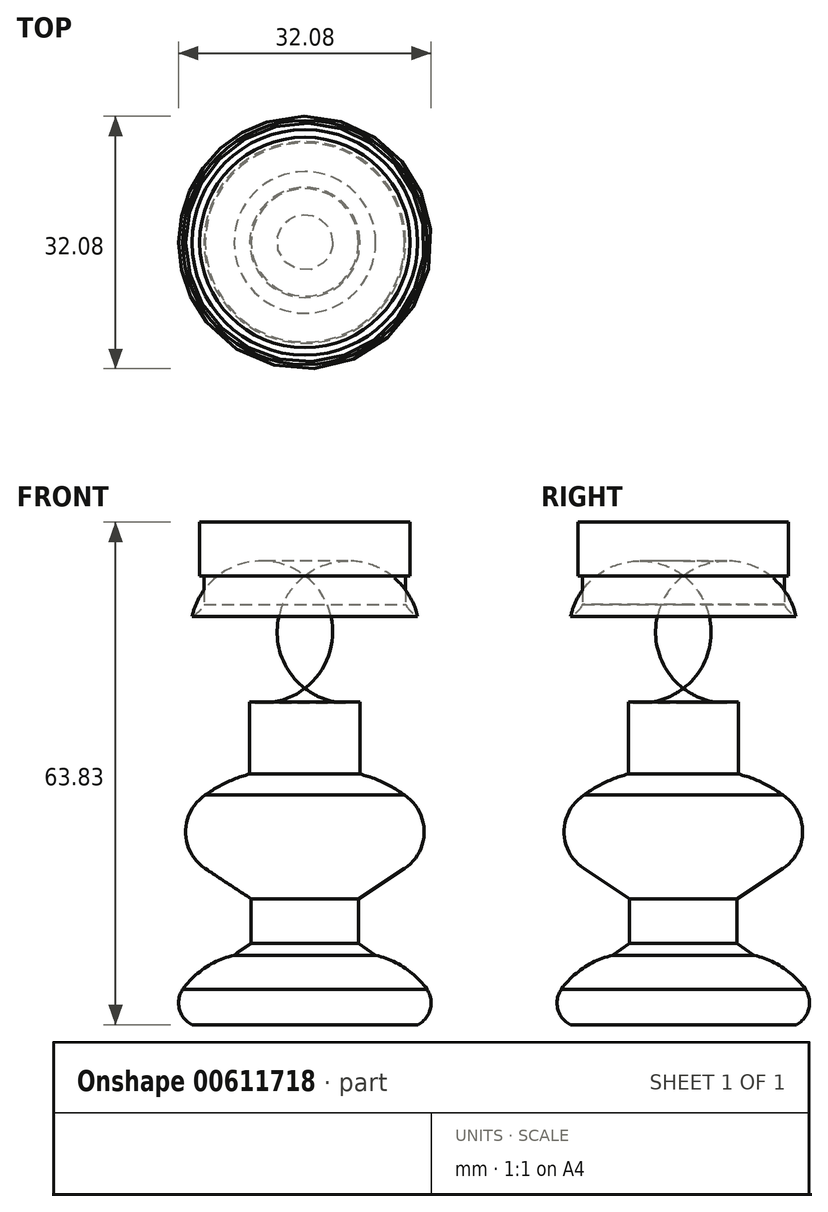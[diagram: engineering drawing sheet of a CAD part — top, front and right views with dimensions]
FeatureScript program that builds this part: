
annotation { "Feature Type Name" : "Feature", "Feature Type Description" : "" }
export const myFeature = defineFeature(function(context is Context, id is Id, definition is map)
    precondition{}
    {
        {
            var Q0;
            Q0=qCreatedBy(makeId("Front.planeOp"),FACE);
            var sketch = newSketch(context, id + "F0", { "sketchPlane" : qUnion([Q0])});
            skLineSegment(sketch, "E0", {"start": v(0, -25.19) * mm, "end": v(-14.34, -25.19) * mm});
            skArc(sketch, "E1", {"start": v(-15.5, -20.69) * mm, "mid": v(-15.94, -23.2) * mm, "end": v(-14.34, -25.19) * mm});
            skArc(sketch, "E2", {"start": v(-9, -16.37) * mm, "mid": v(-12.63, -17.95) * mm, "end": v(-15.5, -20.69) * mm});
            skLineSegment(sketch, "E3", {"start": v(-7, 6.65) * mm, "end": v(-7, 15.79) * mm});
            skArc(sketch, "E4", {"start": v(-14.32, 26.67) * mm, "mid": v(-13, 19.65) * mm, "end": v(-7, 15.79) * mm});
            skArc(sketch, "E5", {"start": v(-14.32, 26.67) * mm, "mid": v(-13.43, 27.3) * mm, "end": v(-12.8, 28.22) * mm});
            skLineSegment(sketch, "E6", {"start": v(-12.8, 28.22) * mm, "end": v(-12.8, 31.52) * mm});
            skArc(sketch, "E7", {"start": v(-12.8, 31.52) * mm, "mid": v(-13, 31.83) * mm, "end": v(-13.36, 31.79) * mm});
            skLineSegment(sketch, "E8", {"start": v(-13.36, 31.79) * mm, "end": v(-13.36, 38.64) * mm});
            skLineSegment(sketch, "E9", {"start": v(-13.36, 38.64) * mm, "end": v(0, 38.64) * mm});
            skLineSegment(sketch, "E10", {"start": v(-9, -16.37) * mm, "end": v(-6.82, -14.84) * mm});
            skLineSegment(sketch, "E11", {"start": v(-6.82, -14.84) * mm, "end": v(-6.82, -9.2) * mm});
            skLineSegment(sketch, "E12", {"start": v(-6.82, -9.2) * mm, "end": v(-12.64, -5.35) * mm});
            skArc(sketch, "E13", {"start": v(-12.64, 3.97) * mm, "mid": v(-15.16, -0.7) * mm, "end": v(-12.64, -5.35) * mm});
            skArc(sketch, "E14", {"start": v(-7, 6.65) * mm, "mid": v(-9.95, 5.58) * mm, "end": v(-12.64, 3.97) * mm});
            skLineSegment(sketch, "E15", {"start": v(0, 38.64) * mm, "end": v(0, -26.17) * mm});
            skSolve(sketch);
        }
        {
            var Q0;
            Q0 = qSketchRegion(id + "F0", true);
            var Q1;
            Q1=sQuery(id+"F0.wireOp",EDGE,"E12");
            var Q2;
            Q2=sQuery(id+"F0.wireOp",EDGE,"E13");
            var Q3;
            Q3=sQuery(id+"F0.wireOp",EDGE,"E14");
            var Q4;
            Q4=sQuery(id+"F0.wireOp",EDGE,"E3");
            var Q5;
            Q5=sQuery(id+"F0.wireOp",EDGE,"E4");
            var Q6;
            Q6=sQuery(id+"F0.wireOp",EDGE,"E5");
            var Q7;
            Q7=sQuery(id+"F0.wireOp",EDGE,"E6");
            var Q8;
            Q8=sQuery(id+"F0.wireOp",EDGE,"E7");
            var Q9;
            Q9=sQuery(id+"F0.wireOp",EDGE,"E8");
            var Q10;
            Q10=sQuery(id+"F0.wireOp",EDGE,"E9");
            var Q11;
            Q11=sQuery(id+"F0.wireOp",EDGE,"E11");
            var Q12;
            Q12=sQuery(id+"F0.wireOp",EDGE,"E10");
            var Q13;
            Q13=sQuery(id+"F0.wireOp",EDGE,"E2");
            var Q14;
            Q14=sQuery(id+"F0.wireOp",EDGE,"E1");
            var Q15;
            Q15=sQuery(id+"F0.wireOp",EDGE,"E0");
            var Q16;
            Q16=sQuery(id+"F0.wireOp",EDGE,"E15");
            revolve(context, id + "F1", {"bodyType" : ToolBodyType.SURFACE, "entities" : qUnion([Q0]), "surfaceEntities" : qUnion([Q1, Q2, Q3, Q4, Q5, Q6, Q7, Q8, Q9, Q10, Q11, Q12, Q13, Q14, Q15]), "axis" : qUnion([Q16]), "revolveType" : RevolveType.FULL});
        }
    });
